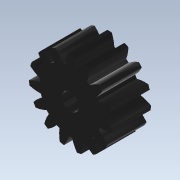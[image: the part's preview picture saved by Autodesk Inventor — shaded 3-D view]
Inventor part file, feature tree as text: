
AUTODESK INVENTOR PART (.ipt)
format: ipt  version: 2020.2 (Build 242310000, 310)  size: 219,648 bytes
history: native  units: mm (DEFAULTED — no unit token found)
features: other x4, plane x3, sketch x3, extrude x2, direct_edit x1
ambient origin geometry x8: Origin, YZ Plane, XZ Plane, XY Plane, X Axis, Y Axis, Z Axis, Center Point
bodies: Solid1 (feature_tree)
feature tree (13):
  extrude  "Extrusion1"  Depth=8.0mm TaperAngle=0.0deg
  plane  "Work Plane2"
  plane  "Work Plane8"
  plane  "Work Plane9"
  other  "Spur Gear"
  extrude  "Extrusion2"  Depth=10.0mm TaperAngle=0.0deg
  direct_edit  "Direct Edit1"
  sketch  "Sketch1"  dims[d0=17.0mm d1=8.0mm d2=0.0mm]
  sketch  "Sketch2"  dims[d3=15.0mm d4=10.0mm d5=0.0mm]
  other  "Srf1"
  sketch  "Sketch3"  dims[d16=15.0mm d17=0.0mm d34=2.094395mm d39=0.0mm d41=0.0mm d43=15.0mm d46=15.0mm d47=0.0mm d48=0.0mm d49=2.2mm d50=0.0mm d51=0.0mm d52=9.5mm d53=10.0mm d54=10.0mm]
  other  "Pitch Diameter"
  other  "Scale1"
